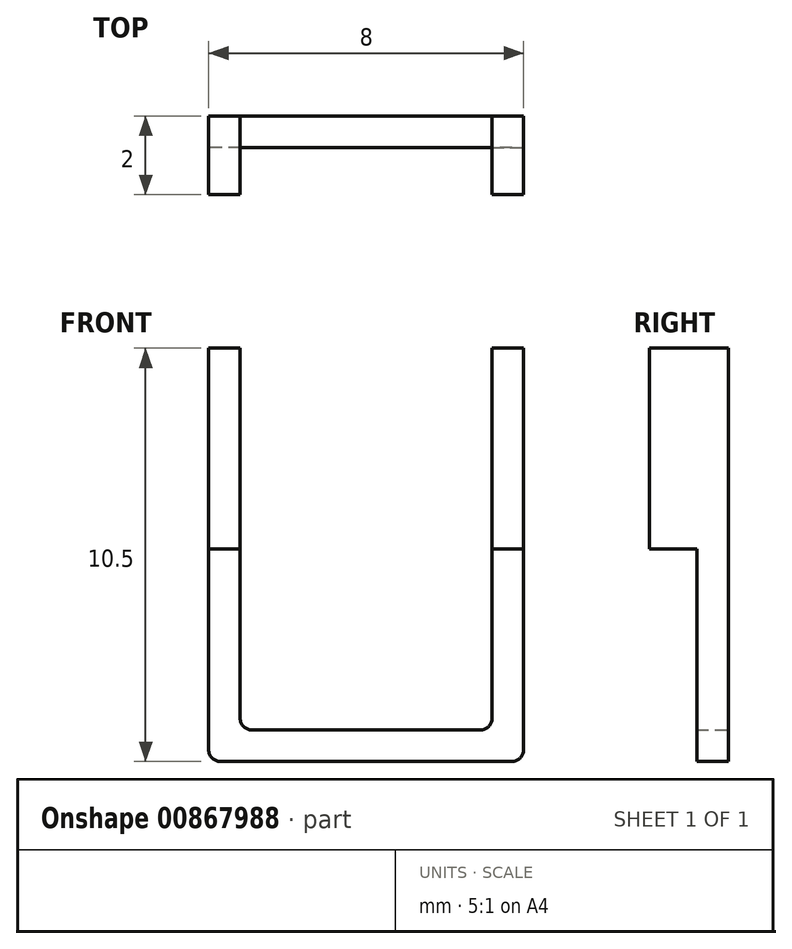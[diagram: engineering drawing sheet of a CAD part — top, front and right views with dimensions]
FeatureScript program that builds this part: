
annotation { "Feature Type Name" : "Feature", "Feature Type Description" : "" }
export const myFeature = defineFeature(function(context is Context, id is Id, definition is map)
    precondition{}
    {
        {
            var Q0;
            Q0=qCreatedBy(makeId("Front.planeOp"),FACE);
            var sketch = newSketch(context, id + "F0", { "sketchPlane" : qUnion([Q0])});
            skLineSegment(sketch, "E0", {"start": v(0, 0) * mm, "end": v(3.2, 0) * mm});
            skLineSegment(sketch, "E1", {"start": v(3.2, 0) * mm, "end": v(3.2, 9.7) * mm});
            skLineSegment(sketch, "E2", {"start": v(3.2, 9.7) * mm, "end": v(4, 9.7) * mm});
            skLineSegment(sketch, "E3", {"start": v(4, 9.7) * mm, "end": v(4, -0.8) * mm});
            skLineSegment(sketch, "E4", {"start": v(4, -0.8) * mm, "end": v(0, -0.8) * mm});
            skLineSegment(sketch, "E5", {"start": v(0, -0.8) * mm, "end": v(0, 0) * mm});
            skSolve(sketch);
        }
        {
            var Q0;
            Q0=makeQuery(id+"F0.imprint","IMPRINT",FACE,{"disambiguationData":[TD([[makeQuery(id+"F0.imprint","IMPRINT",EDGE,{"derivedFrom":sQuery(id+"F0.wireOp",EDGE,"E0")}),-1.0]])]});
            extrude(context, id + "F1", {"entities" : qUnion([Q0]), "depth" : 0.8 * mm, "offsetDistance" : 25 * mm});
        }
        {
            var Q0;
            Q0=makeQuery(id+"F1.opExtrude","SWEPT_EDGE",EDGE,{"disambiguationData":[OSD([sQuery(id+"F0.wireOp",EDGE,"E0"),sQuery(id+"F0.wireOp",EDGE,"E1")])]});
            var Q1;
            Q1=makeQuery(id+"F1.opExtrude","SWEPT_EDGE",EDGE,{"disambiguationData":[OSD([sQuery(id+"F0.wireOp",EDGE,"E3"),sQuery(id+"F0.wireOp",EDGE,"E4")])]});
            fillet(context, id + "F2", {"entities" : qUnion([Q0, Q1]), "radius" : 0.3 * mm, "tangentPropagation" : true, "allowEdgeOverflow" : false});
        }
        {
            var Q0;
            Q0=makeQuery(id+"F1.opExtrude","CAP_FACE",FACE,{"disambiguationData":[OSD([sQuery(id+"F0.wireOp",EDGE,"E0"),sQuery(id+"F0.wireOp",EDGE,"E1"),sQuery(id+"F0.wireOp",EDGE,"E2"),sQuery(id+"F0.wireOp",EDGE,"E3"),sQuery(id+"F0.wireOp",EDGE,"E4"),sQuery(id+"F0.wireOp",EDGE,"E5")])],"isStart":false});
            var sketch = newSketch(context, id + "F3", { "sketchPlane" : qUnion([Q0])});
            skLineSegment(sketch, "E6.bottom", {"start": v(3.2, 9.7) * mm, "end": v(4, 9.7) * mm});
            skLineSegment(sketch, "E6.top", {"start": v(3.2, 4.6) * mm, "end": v(4, 4.6) * mm});
            skLineSegment(sketch, "E6.left", {"start": v(3.2, 9.7) * mm, "end": v(3.2, 4.6) * mm});
            skLineSegment(sketch, "E6.right", {"start": v(4, 9.7) * mm, "end": v(4, 4.6) * mm});
            skSolve(sketch);
        }
        {
            var Q0;
            Q0=makeQuery(id+"F3.imprint","IMPRINT",FACE,{"disambiguationData":[TD([[makeQuery(id+"F3.imprint","IMPRINT",EDGE,{"derivedFrom":sQuery(id+"F3.wireOp",EDGE,"E6.bottom")}),-1.0]])]});
            extrude(context, id + "F4", {"entities" : qUnion([Q0]), "operationType" : NewBodyOperationType.ADD, "depth" : 1.2 * mm, "offsetDistance" : 25 * mm});
        }
        {
            var Q0;
            Q0=makeQuery(id+"F1.opExtrude","SWEPT_BODY",BODY,{"disambiguationData":[OSD([sQuery(id+"F0.wireOp",EDGE,"E0"),sQuery(id+"F0.wireOp",EDGE,"E1"),sQuery(id+"F0.wireOp",EDGE,"E2"),sQuery(id+"F0.wireOp",EDGE,"E3"),sQuery(id+"F0.wireOp",EDGE,"E4"),sQuery(id+"F0.wireOp",EDGE,"E5")])]});
            var Q1;
            Q1=makeQuery(id+"F1.opExtrude","SWEPT_FACE",FACE,{"disambiguationData":[OSD([sQuery(id+"F0.wireOp",EDGE,"E5")])]});
            mirror(context, id + "F5", {"operationType" : NewBodyOperationType.ADD, "entities" : qUnion([Q0]), "mirrorPlane" : qUnion([Q1])});
        }
    });
